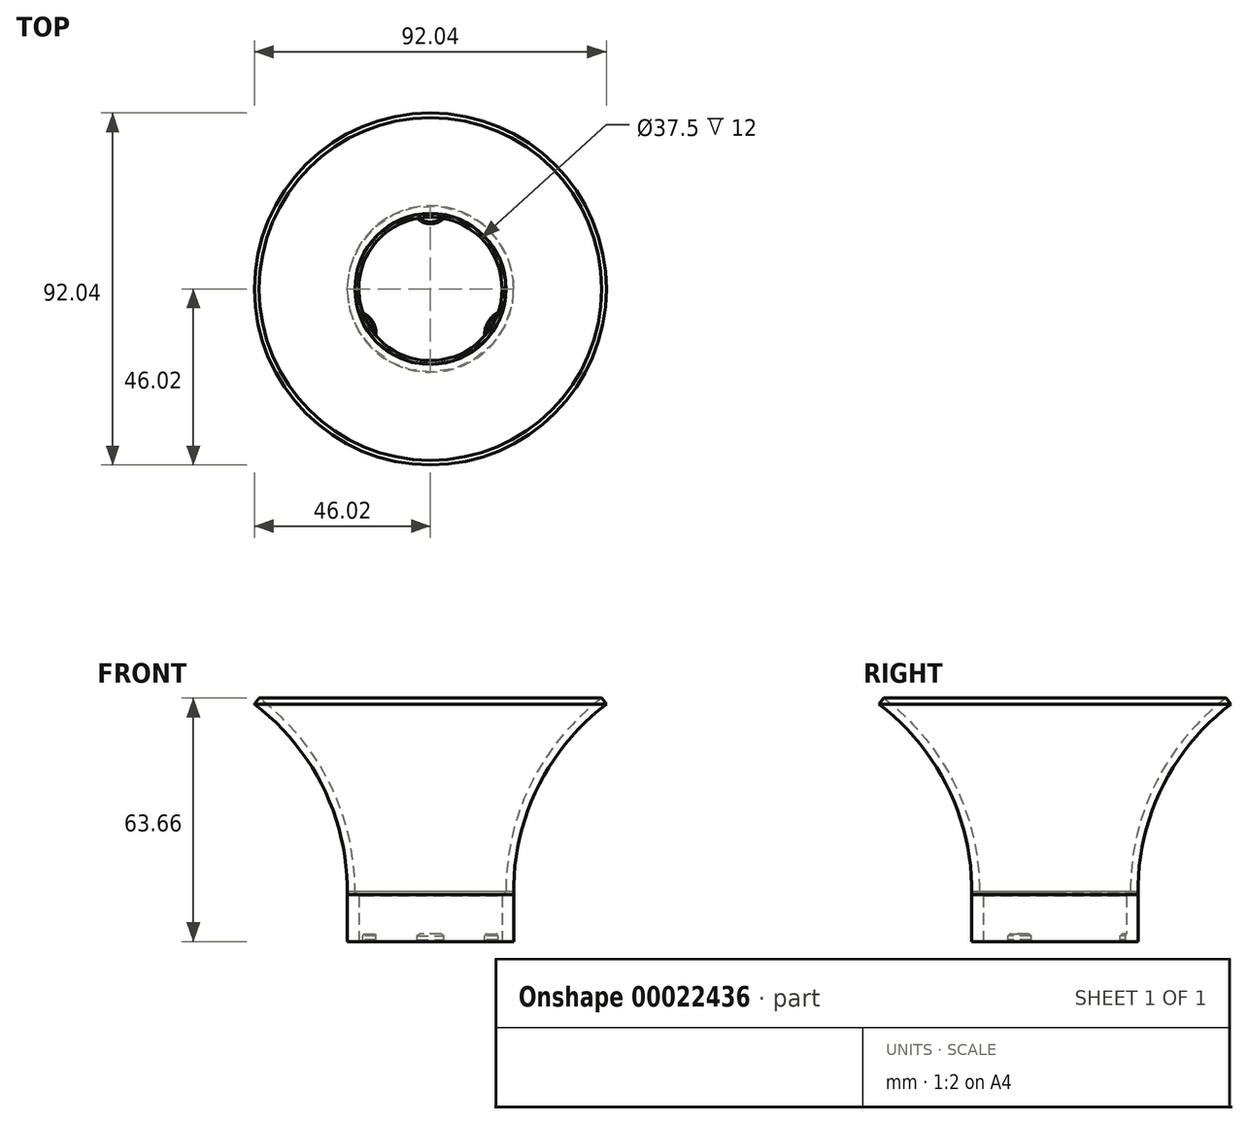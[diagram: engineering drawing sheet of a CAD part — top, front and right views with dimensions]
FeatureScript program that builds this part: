
annotation { "Feature Type Name" : "Feature", "Feature Type Description" : "" }
export const myFeature = defineFeature(function(context is Context, id is Id, definition is map)
    precondition{}
    {
        {
            var Q0;
            Q0=qCreatedBy(makeId("Top.planeOp"),FACE);
            var sketch = newSketch(context, id + "F0", { "sketchPlane" : qUnion([Q0])});
            skCircle(sketch, "E0", {"center": v(0, 0) * mm, "radius": 18.75 * mm});
            skArc(sketch, "E1", {"start": v(-14.2, -12.24) * mm, "mid": v(-15.03, -8.68) * mm, "end": v(-17.7, -6.18) * mm});
            skArc(sketch, "E2", {"start": v(-3.5, 18.42) * mm, "mid": v(0, 17.03) * mm, "end": v(3.5, 18.42) * mm});
            skArc(sketch, "E3", {"start": v(17.7, -6.18) * mm, "mid": v(15.06, -8.7) * mm, "end": v(14.2, -12.24) * mm});
            skCircle(sketch, "E4.0", {"center": v(0, 0) * mm, "radius": 21.75 * mm});
            skSolve(sketch);
        }
        {
            var Q0;
            Q0=makeQuery(id+"F0.imprint","IMPRINT",FACE,{"disambiguationData":[TD([[makeQuery(id+"F0.imprint","IMPRINT",EDGE,{"derivedFrom":sQuery(id+"F0.wireOp",EDGE,"E4.0")}),1.0]])]});
            extrude(context, id + "F1", {"entities" : qUnion([Q0]), "depth" : 11 * mm});
        }
        {
            var Q0;
            Q0=makeQuery(id+"F0.imprint","IMPRINT",FACE,{"disambiguationData":[TD([[makeQuery(id+"F0.imprint","IMPRINT",EDGE,{"derivedFrom":sQuery(id+"F0.wireOp",EDGE,"E4.0")}),1.0]])]});
            var Q1;
            {var subQ0=sQuery(id+"F0.wireOp",EDGE,"E1");Q1=makeQuery(id+"F0.imprint","IMPRINT",FACE,{"disambiguationData":[TD([[makeQuery(id+"F0.imprint","IMPRINT",EDGE,{"derivedFrom":subQ0}),1.0]])]});}
            var Q2;
            {var subQ0=sQuery(id+"F0.wireOp",EDGE,"E3");Q2=makeQuery(id+"F0.imprint","IMPRINT",FACE,{"disambiguationData":[TD([[makeQuery(id+"F0.imprint","IMPRINT",EDGE,{"derivedFrom":subQ0}),1.0]])]});}
            var Q3;
            {var subQ0=sQuery(id+"F0.wireOp",EDGE,"E2");Q3=makeQuery(id+"F0.imprint","IMPRINT",FACE,{"disambiguationData":[TD([[makeQuery(id+"F0.imprint","IMPRINT",EDGE,{"derivedFrom":subQ0}),1.0]])]});}
            extrude(context, id + "F2", {"entities" : qUnion([Q0, Q1, Q2, Q3]), "operationType" : NewBodyOperationType.ADD, "oppositeDirection" : true, "depth" : 2 * mm});
        }
        {
            var Q0;
            Q0=makeQuery(id+"F2.opExtrude","CAP_EDGE",EDGE,{"disambiguationData":[OSD([sQuery(id+"F0.wireOp",EDGE,"E2")])],"isStart":true});
            var Q1;
            Q1=makeQuery(id+"F2.opExtrude","CAP_EDGE",EDGE,{"disambiguationData":[OSD([sQuery(id+"F0.wireOp",EDGE,"E2")])],"isStart":false});
            var Q2;
            Q2=makeQuery(id+"F2.opExtrude","CAP_EDGE",EDGE,{"disambiguationData":[OSD([sQuery(id+"F0.wireOp",EDGE,"E1")])],"isStart":false});
            var Q3;
            Q3=makeQuery(id+"F2.opExtrude","CAP_EDGE",EDGE,{"disambiguationData":[OSD([sQuery(id+"F0.wireOp",EDGE,"E1")])],"isStart":true});
            var Q4;
            Q4=makeQuery(id+"F2.opExtrude","CAP_EDGE",EDGE,{"disambiguationData":[OSD([sQuery(id+"F0.wireOp",EDGE,"E3")])],"isStart":true});
            var Q5;
            Q5=makeQuery(id+"F2.opExtrude","CAP_EDGE",EDGE,{"disambiguationData":[OSD([sQuery(id+"F0.wireOp",EDGE,"E3")])],"isStart":false});
            chamfer(context, id + "F3", {"entities" : qUnion([Q0, Q1, Q2, Q3, Q4, Q5]), "width" : .5 * mm, "tangentPropagation" : true});
        }
        {
            var Q0;
            Q0=qCreatedBy(makeId("Top.planeOp"),FACE);
            cPlane(context, id + "F4", {"entities" : qUnion([Q0]), "cplaneType" : CPlaneType.OFFSET, "offset" : 60 * mm, "width" : 150 * mm, "height" : 150 * mm});
        }
        {
            var Q0;
            Q0=qCreatedBy(makeId("Front.planeOp"),FACE);
            var sketch = newSketch(context, id + "F5", { "sketchPlane" : qUnion([Q0])});
            skLineSegment(sketch, "E5", {"start": v(0, 0) * mm, "end": v(0, 68.34) * mm});
            skArc(sketch, "E6", {"start": v(-21.76, 10.26) * mm, "mid": v(-27.93, 38.07) * mm, "end": v(-46.02, 60.06) * mm});
            skArc(sketch, "E7.0", {"start": v(-19.76, 10.22) * mm, "mid": v(-26.13, 38.94) * mm, "end": v(-44.82, 61.66) * mm});
            skLineSegment(sketch, "E8", {"start": v(-46.02, 60.06) * mm, "end": v(-44.82, 61.66) * mm});
            skLineSegment(sketch, "E9", {"start": v(-19.76, 10.22) * mm, "end": v(-21.76, 10.26) * mm});
            skSolve(sketch);
        }
        {
            var Q0;
            Q0 = qSketchRegion(id + "F5", true);
            var Q1;
            Q1=sQuery(id+"F5.wireOp",EDGE,"E5");
            revolve(context, id + "F6", {"entities" : qUnion([Q0]), "axis" : qUnion([Q1]), "revolveType" : RevolveType.FULL});
        }
        {
            var Q0;
            Q0=makeQuery(id+"F1.opExtrude","CAP_EDGE",EDGE,{"disambiguationData":[OSD([sQuery(id+"F0.wireOp",EDGE,"E0")])],"isStart":false});
            chamfer(context, id + "F7", {"entities" : qUnion([Q0]), "width" : 1 * mm, "tangentPropagation" : true});
        }
    });
